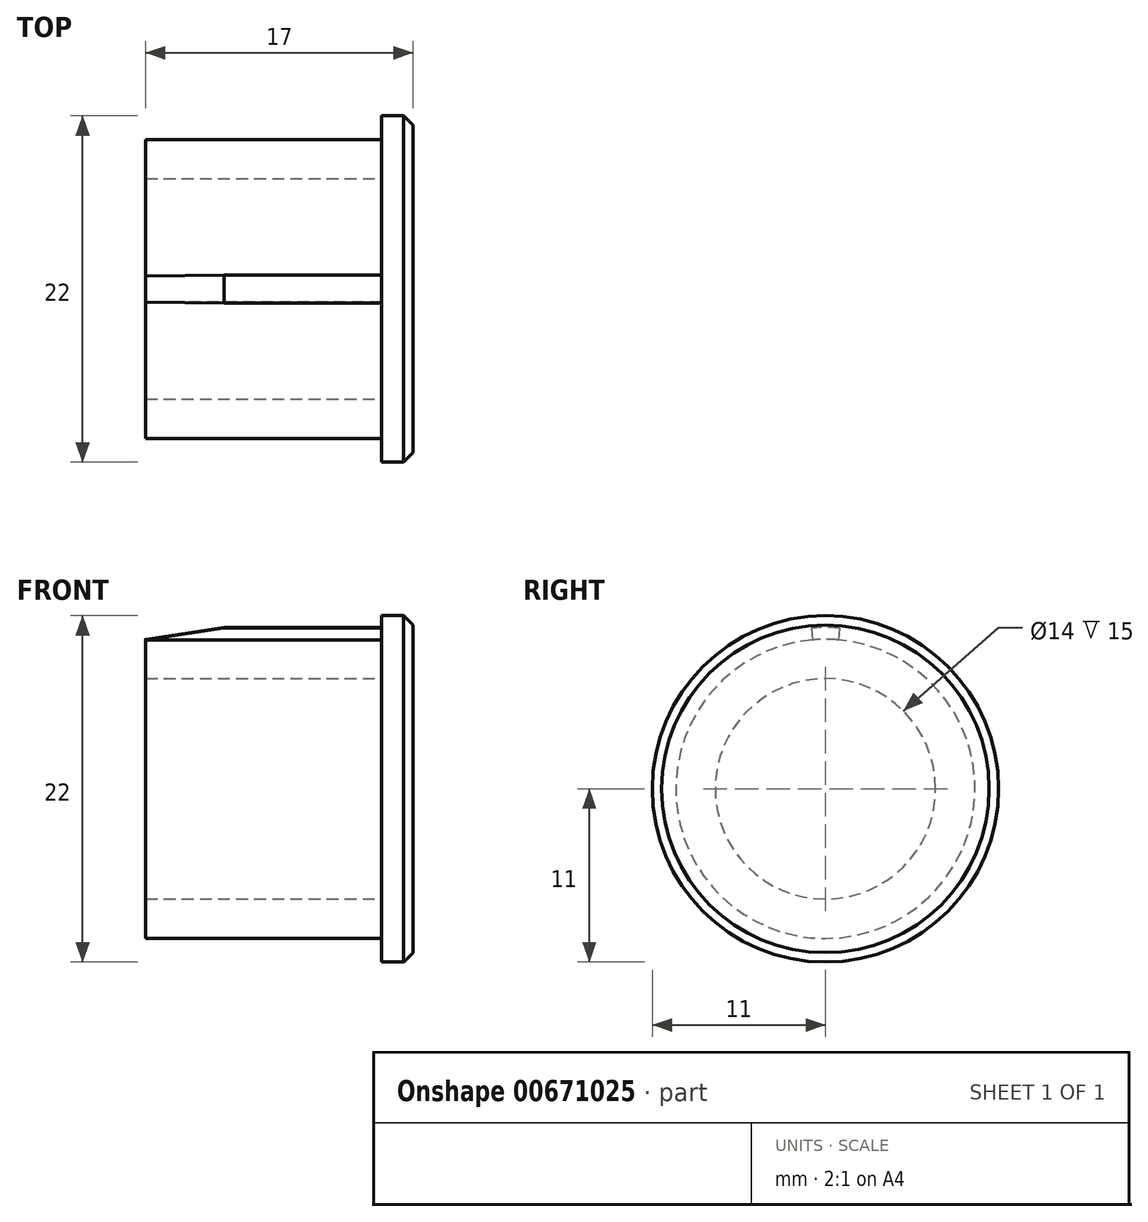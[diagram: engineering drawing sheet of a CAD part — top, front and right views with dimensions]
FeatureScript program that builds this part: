
annotation { "Feature Type Name" : "Feature", "Feature Type Description" : "" }
export const myFeature = defineFeature(function(context is Context, id is Id, definition is map)
    precondition{}
    {
        {
            var Q0;
            Q0=qCreatedBy(makeId("Front.planeOp"),FACE);
            var sketch = newSketch(context, id + "F0", { "sketchPlane" : qUnion([Q0])});
            skLineSegment(sketch, "E0", {"start": v(0, 0) * mm, "end": v(0, 11) * mm});
            skLineSegment(sketch, "E1", {"start": v(0, 11) * mm, "end": v(-2, 11) * mm});
            skLineSegment(sketch, "E2", {"start": v(-2, 11) * mm, "end": v(-2, 9.5) * mm});
            skLineSegment(sketch, "E3", {"start": v(-2, 9.5) * mm, "end": v(-17, 9.5) * mm});
            skLineSegment(sketch, "E4", {"start": v(-17, 9.5) * mm, "end": v(-17, 7) * mm});
            skLineSegment(sketch, "E5", {"start": v(-17, 7) * mm, "end": v(-2, 7) * mm});
            skLineSegment(sketch, "E6", {"start": v(-2, 7) * mm, "end": v(-2, 0) * mm});
            skLineSegment(sketch, "E7", {"start": v(-2, 0) * mm, "end": v(0, 0) * mm});
            skLineSegment(sketch, "E8", {"start": v(0, 0) * mm, "end": v(-17, 0) * mm, "construction": true});
            skLineSegment(sketch, "E9", {"start": v(-17, 9.5) * mm, "end": v(-12, 10.25) * mm});
            skLineSegment(sketch, "E10", {"start": v(-12, 10.25) * mm, "end": v(-2, 10.25) * mm});
            skSolve(sketch);
        }
        {
            var Q0;
            Q0=makeQuery(id+"F0.imprint","IMPRINT",FACE,{"disambiguationData":[TD([[makeQuery(id+"F0.imprint","IMPRINT",EDGE,{"derivedFrom":sQuery(id+"F0.wireOp",EDGE,"E0")}),1.0]])]});
            var Q1;
            Q1=sQuery(id+"F0.wireOp",EDGE,"E8");
            revolve(context, id + "F1", {"entities" : qUnion([Q0]), "axis" : qUnion([Q1]), "revolveType" : RevolveType.FULL});
        }
        {
            var Q0;
            {var subQ0=sQuery(id+"F0.wireOp",EDGE,"E3");Q0=makeQuery(id+"F0.imprint","IMPRINT",FACE,{"disambiguationData":[TD([[makeQuery(id+"F0.imprint","IMPRINT",EDGE,{"derivedFrom":subQ0}),-1.0]])]});}
            var Q1;
            Q1=sQuery(id+"F0.wireOp",EDGE,"E8");
            revolve(context, id + "F2", {"operationType" : NewBodyOperationType.ADD, "entities" : qUnion([Q0]), "axis" : qUnion([Q1]), "revolveType" : RevolveType.SYMMETRIC, "angle" : 10 * degree});
        }
        {
            var Q0;
            Q0=makeQuery(id+"F1.opRevolve","SWEPT_FACE",FACE,{"disambiguationData":[OSD([sQuery(id+"F0.wireOp",EDGE,"E0")])]});
            chamfer(context, id + "F3", {"entities" : qUnion([Q0]), "width" : 0.6 * mm, "tangentPropagation" : true});
        }
    });
